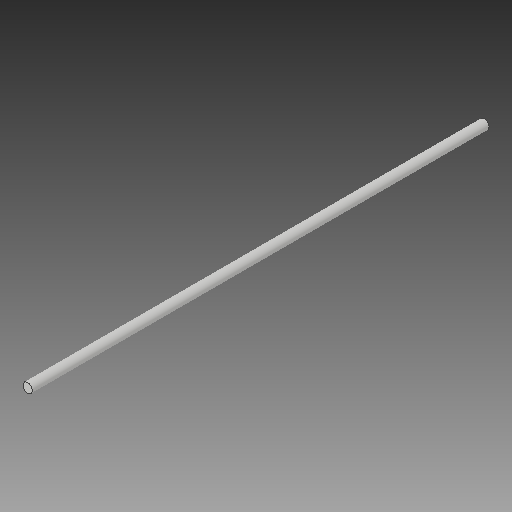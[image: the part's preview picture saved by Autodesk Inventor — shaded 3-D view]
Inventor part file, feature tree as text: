
AUTODESK INVENTOR PART (.ipt)
format: ipt  version: 2019 (Build 230136000, 136)  size: 92,672 bytes
history: native  units: in
note: dims shown in document units (in); Inventor stores cm internally (conversion verified against a paired STEP export)
features: extrude x1, sketch x1
ambient origin geometry x8: Origin, YZ Plane, XZ Plane, XY Plane, X Axis, Y Axis, Z Axis, Center Point
bodies: Solid1 (feature_tree)
feature tree (2):
  extrude  "Extrusion1"  Depth=24.0in TaperAngle=0.0deg
  sketch  "Sketch1"  dims[d0=0.5in d1=24.0in d2=0.0in]
